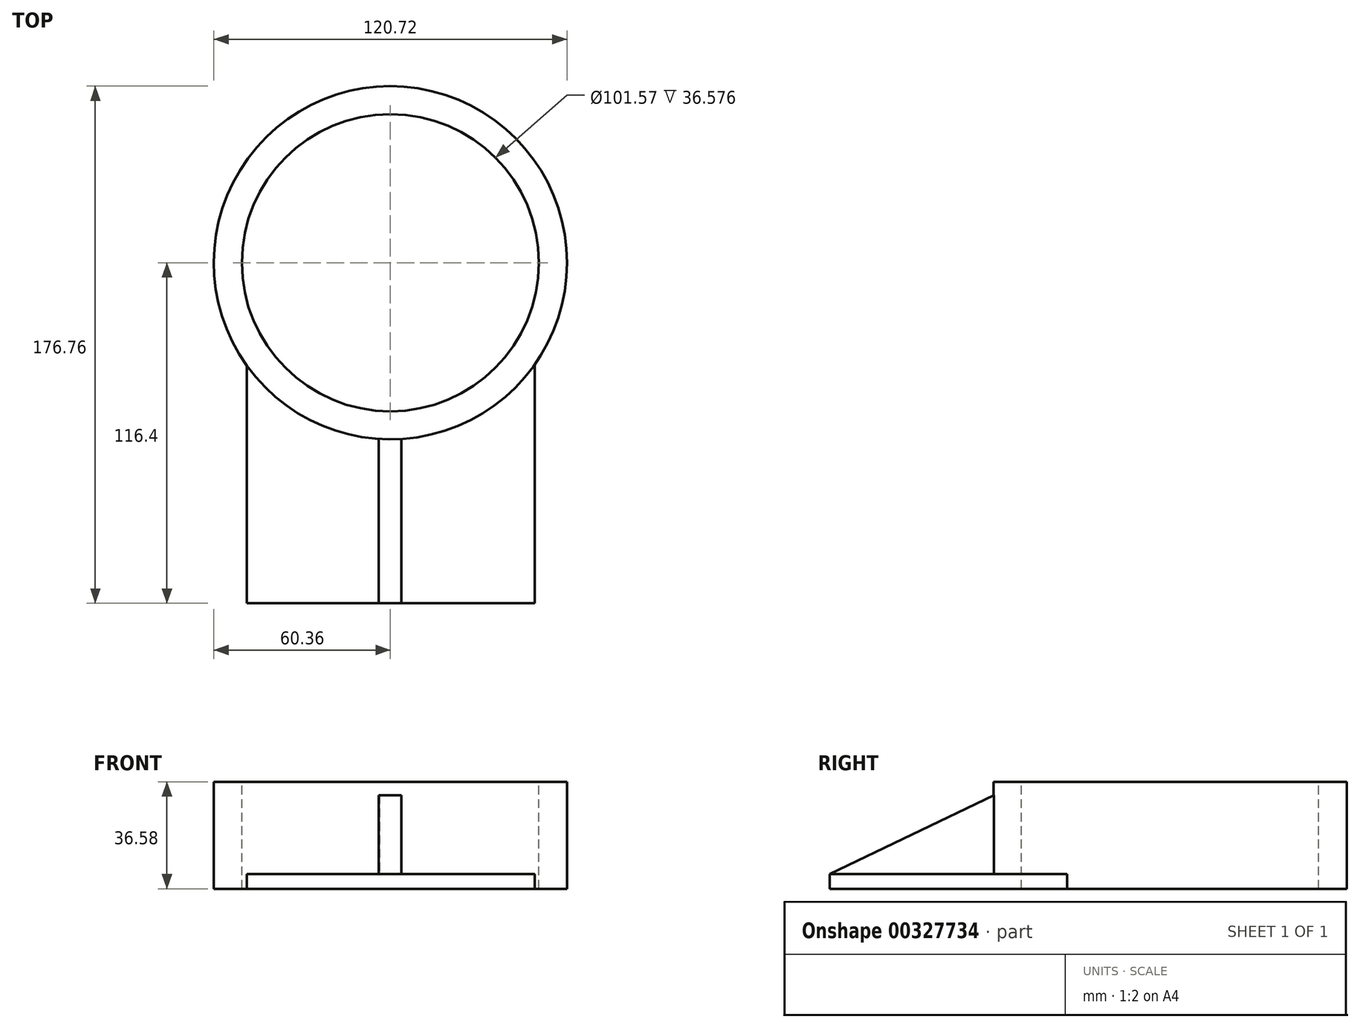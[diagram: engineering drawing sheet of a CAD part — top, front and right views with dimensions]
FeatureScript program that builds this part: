
annotation { "Feature Type Name" : "Feature", "Feature Type Description" : "" }
export const myFeature = defineFeature(function(context is Context, id is Id, definition is map)
    precondition{}
    {
        {
            var Q0;
            Q0=qCreatedBy(makeId("Top.planeOp"),FACE);
            var sketch = newSketch(context, id + "F0", { "sketchPlane" : qUnion([Q0])});
            skCircle(sketch, "E0", {"center": v(0, 0) * mm, "radius": 60.36 * mm});
            skSolve(sketch);
        }
        {
            var Q0;
            Q0=makeQuery(id+"F0.imprint","IMPRINT",FACE,{"disambiguationData":[TD([[makeQuery(id+"F0.imprint","IMPRINT",EDGE,{"derivedFrom":sQuery(id+"F0.wireOp",EDGE,"E0")}),1.0]])]});
            extrude(context, id + "F1", {"entities" : qUnion([Q0]), "depth" : 36.58 * mm});
        }
        {
            var Q0;
            Q0=qCreatedBy(makeId("Top.planeOp"),FACE);
            var sketch = newSketch(context, id + "F2", { "sketchPlane" : qUnion([Q0])});
            skLineSegment(sketch, "E1.bottom", {"start": v(-49.02, -35.15) * mm, "end": v(49.33, -35.15) * mm});
            skLineSegment(sketch, "E1.top", {"start": v(-49.02, -101.16) * mm, "end": v(49.33, -101.16) * mm});
            skLineSegment(sketch, "E1.left", {"start": v(-49.02, -35.15) * mm, "end": v(-49.02, -101.16) * mm});
            skLineSegment(sketch, "E1.right", {"start": v(49.33, -35.15) * mm, "end": v(49.33, -101.16) * mm});
            skSolve(sketch);
        }
        {
            var Q0;
            Q0=makeQuery(id+"F2.imprint","IMPRINT",FACE,{"disambiguationData":[TD([[makeQuery(id+"F2.imprint","IMPRINT",EDGE,{"derivedFrom":sQuery(id+"F2.wireOp",EDGE,"E1.bottom")}),-1.0]])]});
            extrude(context, id + "F3", {"entities" : qUnion([Q0]), "operationType" : NewBodyOperationType.ADD, "depth" : 5.08 * mm});
        }
        {
            var Q0;
            Q0=makeQuery(id+"F1.opExtrude","CAP_FACE",FACE,{"disambiguationData":[OSD([sQuery(id+"F0.wireOp",EDGE,"E0")])],"isStart":false});
            var sketch = newSketch(context, id + "F4", { "sketchPlane" : qUnion([Q0])});
            skCircle(sketch, "E2", {"center": v(0, 0) * mm, "radius": 50.79 * mm});
            skSolve(sketch);
        }
        {
            var Q0;
            Q0=makeQuery(id+"F4.imprint","IMPRINT",FACE,{"disambiguationData":[TD([[makeQuery(id+"F4.imprint","IMPRINT",EDGE,{"derivedFrom":sQuery(id+"F4.wireOp",EDGE,"E2")}),1.0]])]});
            extrude(context, id + "F5", {"entities" : qUnion([Q0]), "operationType" : NewBodyOperationType.REMOVE, "oppositeDirection" : true, "depth" : 63.75 * mm});
        }
        {
            var Q0;
            Q0=makeQuery(id+"F3.opExtrude","SWEPT_FACE",FACE,{"disambiguationData":[OSD([sQuery(id+"F2.wireOp",EDGE,"E1.top")])]});
            extrude(context, id + "F6", {"entities" : qUnion([Q0]), "operationType" : NewBodyOperationType.ADD, "depth" : 15.24 * mm});
        }
        {
            var Q0;
            {var subQ0=sQuery(id+"F2.wireOp",EDGE,"E1.top");Q0=makeQuery(id+"F6.boolean.opBoolean","MERGE",FACE,{"derivedFrom":[makeQuery(id+"F3.opExtrude","CAP_FACE",FACE,{"disambiguationData":[OSD([sQuery(id+"F2.wireOp",EDGE,"E1.bottom"),subQ0,sQuery(id+"F2.wireOp",EDGE,"E1.left"),sQuery(id+"F2.wireOp",EDGE,"E1.right")])],"isStart":false}),makeQuery(id+"F6.opExtrude","SWEPT_FACE",FACE,{"disambiguationData":[OSD([subQ0]),TDD([makeQuery(id+"F3.opExtrude","CAP_EDGE",EDGE,{"disambiguationData":[OSD([subQ0])],"isStart":false})])]})]});}
            var sketch = newSketch(context, id + "F7", { "sketchPlane" : qUnion([Q0])});
            skLineSegment(sketch, "E3.bottom", {"start": v(-3.98, -116.4) * mm, "end": v(3.73, -116.4) * mm});
            skLineSegment(sketch, "E3.top", {"start": v(-3.98, -60.24) * mm, "end": v(3.73, -60.24) * mm});
            skLineSegment(sketch, "E3.left", {"start": v(-3.98, -116.4) * mm, "end": v(-3.98, -60.24) * mm});
            skLineSegment(sketch, "E3.right", {"start": v(3.73, -116.4) * mm, "end": v(3.73, -60.24) * mm});
            skSolve(sketch);
        }
        {
            var Q0;
            Q0=makeQuery(id+"F7.imprint","IMPRINT",FACE,{"disambiguationData":[TD([[makeQuery(id+"F7.imprint","IMPRINT",EDGE,{"derivedFrom":sQuery(id+"F7.wireOp",EDGE,"E3.bottom")}),1.0]])]});
            extrude(context, id + "F8", {"entities" : qUnion([Q0]), "operationType" : NewBodyOperationType.ADD, "depth" : 26.92 * mm});
        }
        {
            var Q0;
            Q0=makeQuery(id+"F8.opExtrude","SWEPT_FACE",FACE,{"disambiguationData":[OSD([sQuery(id+"F7.wireOp",EDGE,"E3.right")])]});
            var sketch = newSketch(context, id + "F9", { "sketchPlane" : qUnion([Q0])});
            skLineSegment(sketch, "E4", {"start": v(-116.4, 5.08) * mm, "end": v(-60.24, 32) * mm});
            skSolve(sketch);
        }
        {
            var Q0;
            Q0=makeQuery(id+"F9.imprint","IMPRINT",FACE,{"disambiguationData":[TD([[makeQuery(id+"F9.imprint","IMPRINT",EDGE,{"derivedFrom":sQuery(id+"F9.wireOp",EDGE,"E4")}),1.0]])]});
            extrude(context, id + "F10", {"entities" : qUnion([Q0]), "operationType" : NewBodyOperationType.REMOVE, "oppositeDirection" : true, "depth" : 61.72 * mm});
        }
    });
